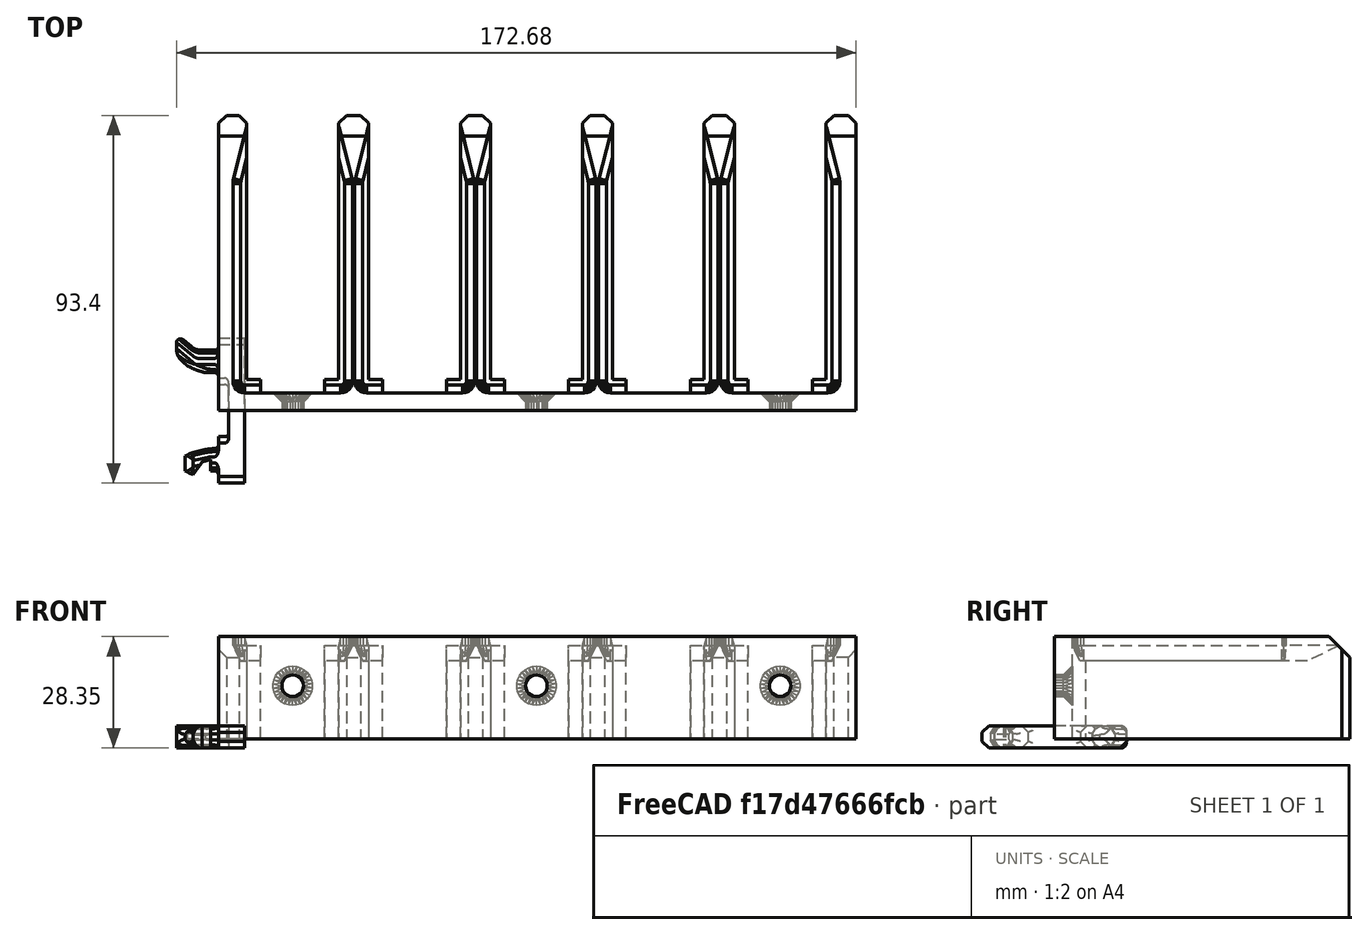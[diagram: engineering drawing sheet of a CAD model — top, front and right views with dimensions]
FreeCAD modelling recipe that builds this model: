
FCSTD DOCUMENT  (FreeCAD 0.21R33771 (Git))
Label: MultiboardMagRack
License: All rights reserved
objects: PartDesign::CoordinateSystem×3, App::DocumentObjectGroup×3, App::Part×3, App::Link×3, Part::Feature×2, App::FeaturePython×1
note: 5 computed .brp shape members not serialized (recipe doc carries the construction recipe); baked Part::Feature solids carry a one-line shape summary decoded from their .brp

FEATURE [PartDesign::CoordinateSystem] LCS_Origin
  AttacherType = Attacher::AttachEngine3D
  MapMode = 2
  Support = -> [X_Axis001]
FEATURE [App::DocumentObjectGroup] Constraints
FEATURE [App::FeaturePython] Variables  # WARN: FeaturePython — macro-defined, semantics opaque (R4)
  Type = App::PropertyContainer
FEATURE [App::DocumentObjectGroup] Configurations
FEATURE [PartDesign::CoordinateSystem] LCS_0
  AttacherType = Attacher::AttachEngine3D
  MapMode = 2
  Support = -> [X_Axis002]
FEATURE [Part::Feature] Pmag007_solid  label="Pmag007 (Solid)"
  shape: bbox 162 x 75 x 26 mm, 660 faces (baked)
FEATURE [App::Part] MagRack
  Group = -> [LCS_0,Pmag007_solid]
  Origin = -> Origin002
FEATURE [PartDesign::CoordinateSystem] LCS_001
  AttacherType = Attacher::AttachEngine3D
  MapMode = 2
  Support = -> [X_Axis]
FEATURE [Part::Feature] Part__Feature  label="Peg Click"
  shape: bbox 17.3 x 36.82 x 7.448 mm, 118 faces (baked)
FEATURE [App::Part] MultiboardPeg
  Group = -> [LCS_001,Part__Feature]
  Origin = -> Origin
FEATURE [App::DocumentObjectGroup] Parts
  Group = -> [MagRack,MultiboardPeg]
FEATURE [App::Link] MagRack001
  AttachedBy = #LCS_0
  AttachedTo = Parent Assembly#LCS_Origin
  LinkedObject = -> MagRack
  SolverId = Asm4EE
  expr: Placement = LCS_Origin.Placement * AttachmentOffset * LCS_0.Placement ^ -1
FEATURE [App::Link] MultiboardPeg001
  AttachedBy = #LCS_001
  AttachedTo = MagRack001#LCS_0
  AttachmentOffset = pos=(30.5,-6.6,18.5) rot=(0.57735,0.57735,0.57735;2.0944rad)
  LinkPlacement = pos=(30.5,-6.6,18.5) rot=(0.57735,0.57735,0.57735;2.0944rad)
  LinkedObject = -> MultiboardPeg
  Placement = pos=(30.5,-6.6,18.5) rot=(0.57735,0.57735,0.57735;2.0944rad)
  SolverId = Asm4EE
  expr: Placement = MagRack001.Placement * LCS_0.Placement * AttachmentOffset * LCS_001.Placement ^ -1
FEATURE [App::Link] MultiboardPeg002
  AttachedBy = #LCS_001
  AttachedTo = MagRack001#LCS_0
  AttachmentOffset = pos=(130.5,-6.6,18.5) rot=(0.57735,0.57735,0.57735;2.0944rad)
  LinkPlacement = pos=(130.5,-6.6,18.5) rot=(0.57735,0.57735,0.57735;2.0944rad)
  LinkedObject = -> MultiboardPeg
  Placement = pos=(130.5,-6.6,18.5) rot=(0.57735,0.57735,0.57735;2.0944rad)
  SolverId = Asm4EE
  expr: Placement = MagRack001.Placement * LCS_0.Placement * AttachmentOffset * LCS_001.Placement ^ -1
FEATURE [App::Part] Assembly
  AssemblyType = Part::Link
  Group = -> [LCS_Origin,Constraints,Variables,Configurations,MagRack001,MultiboardPeg001,MultiboardPeg002]
  Origin = -> Origin001
  Type = Assembly
